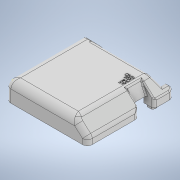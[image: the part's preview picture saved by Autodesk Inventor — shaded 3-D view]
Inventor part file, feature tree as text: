
AUTODESK INVENTOR PART (.ipt)
format: ipt  version: 2022 (Build 260153000, 153)  size: 1,379,840 bytes
history: native  units: mm
features: extrude x58, sketch x43, fillet x10, projected_geometry x2
ambient origin geometry x8: Origin, YZ Plane, XZ Plane, XY Plane, X Axis, Y Axis, Z Axis, Center Point
bodies: Solid1 (feature_tree)
feature tree (113):
  extrude  "Extrusion1"  Depth=62.0mm
  extrude  "Extrusion2"  Depth=3.0mm
  extrude  "Extrusion28"  Depth=3.0mm
  extrude  "Extrusion29"  Depth=4.5mm
  extrude  "Extrusion30"  Depth=3.0mm
  extrude  "Extrusion31"  Depth=54.35mm
  extrude  "Extrusion34"  Depth=51.56mm
  extrude  "Extrusion35"  Depth=6.0mm
  extrude  "Extrusion36"  Depth=6.0mm
  extrude  "Extrusion37"  Depth=20.0mm
  extrude  "Extrusion38"  Depth=1.0mm
  extrude  "Extrusion39"  Depth=2.5mm
  extrude  "Extrusion40"  Depth=2.5mm
  extrude  "Extrusion41"  Depth=3.0mm TaperAngle=0.0deg
  extrude  "Extrusion42"  Depth=8.0mm TaperAngle=0.0deg
  extrude  "Extrusion43"  Depth=8.0mm TaperAngle=0.0deg
  extrude  "Extrusion44"  Depth=2.0mm
  extrude  "Extrusion45"  Depth=4.5mm
  extrude  "Extrusion46"  TaperAngle=0.0deg  [1 undecoded]
  extrude  "Extrusion47"  TaperAngle=0.0deg  [1 undecoded]
  extrude  "Extrusion48"  Depth=2.0mm TaperAngle=0.0deg
  extrude  "Extrusion49"  Depth=10.0mm TaperAngle=0.0deg
  extrude  "Extrusion50"  TaperAngle=0.0deg  [1 undecoded]
  extrude  "Extrusion51"  Depth=2.0mm
  extrude  "Extrusion52"  Depth=3.0mm
  extrude  "Extrusion54"  Depth=3.0mm
  extrude  "Extrusion56"  Depth=2.0mm
  extrude  "Extrusion57"  Depth=2.0mm
  extrude  "Extrusion58"  Depth=2.0mm
  extrude  "Extrusion60"  Depth=8.0mm TaperAngle=0.0deg
  extrude  "Extrusion64"  Depth=4.5mm
  extrude  "Extrusion70"  Depth=4.7mm
  extrude  "Extrusion71"  Depth=100000.0mm TaperAngle=0.0deg
  extrude  "Extrusion72"  Depth=1.0mm
  extrude  "Extrusion73"  Depth=4.7mm
  extrude  "Extrusion74"  Depth=4.7mm
  extrude  "Extrusion75"  Depth=10000.0mm TaperAngle=0.0deg
  extrude  "Extrusion76"  Depth=66.0mm TaperAngle=0.0deg
  extrude  "Extrusion77"  Depth=1000.0mm TaperAngle=0.0deg
  extrude  "Extrusion78"  Depth=67.15mm
  extrude  "Extrusion79"  Depth=1.83mm
  extrude  "Extrusion80"  Depth=1000.0mm TaperAngle=0.0deg
  extrude  "Extrusion81"  Depth=71.5mm
  extrude  "Extrusion82"  Depth=71.5mm
  extrude  "Extrusion83"  Depth=7.0mm TaperAngle=0.0deg
  extrude  "Extrusion84"  Depth=2.0mm
  extrude  "Extrusion85"  Depth=5.0mm TaperAngle=0.0deg
  extrude  "Extrusion86"  Depth=1.0mm TaperAngle=0.0deg
  extrude  "Extrusion89"  TaperAngle=0.0deg  [1 undecoded]
  extrude  "Extrusion90"  Depth=9.0mm
  extrude  "Extrusion91"  Depth=10.0mm TaperAngle=0.0deg
  extrude  "Extrusion92"  Depth=5.65mm
  extrude  "Extrusion93"  Depth=10.0mm TaperAngle=0.0deg
  extrude  "Extrusion94"  Depth=1000.0mm TaperAngle=0.0deg
  extrude  "Extrusion95"  Depth=1000.0mm TaperAngle=0.0deg
  extrude  "Extrusion96"  Depth=1000.0mm TaperAngle=0.0deg
  extrude  "Extrusion97"  Depth=4.0mm
  fillet  "Fillet17"  Radius=1000.0mm
  fillet  "Fillet18"  Radius=4.0mm
  fillet  "Fillet19"  Radius=1000.0mm
  fillet  "Fillet23"  Radius=2.0mm
  fillet  "Fillet26"  Radius=2.0mm
  fillet  "Fillet27"  Radius=2.0mm
  fillet  "Fillet28"  Radius=4.0mm
  fillet  "Fillet29"  Radius=10.0mm
  fillet  "Fillet30"  Radius=1000.0mm
  fillet  "Fillet31"  Radius=2.0mm
  sketch  "Sketch118"  dims[d426=2.0mm d427=0.0mm d432=67.15mm]
  extrude  "Extrusion98"  Depth=2.0mm
  sketch  "Sketch2"  dims[d14=66.0mm d15=62.0mm]
  sketch  "Sketch4"  dims[d16=3.0mm d17=3.0mm]
  sketch  "Sketch38"  dims[d18=3.0mm d19=3.0mm]
  sketch  "Sketch39"  dims[d20=3.0mm d21=4.5mm]
  sketch  "Sketch40"  dims[d22=6.0mm d23=3.0mm]
  sketch  "Sketch47"  dims[d24=57.4mm d25=54.35mm]
  sketch  "Sketch48"  dims[d26=0.8mm d27=51.56mm]
  sketch  "Sketch50"  dims[d28=4.8mm d29=6.0mm]
  sketch  "Sketch51"  dims[d30=6.0mm d31=6.0mm]
  sketch  "Sketch54"  dims[d32=20.0mm d33=20.0mm]
  sketch  "Sketch57"  dims[d34=1.0mm d35=1.0mm]
  sketch  "Sketch59"  dims[d36=2.0mm d37=0.0mm]
  sketch  "Sketch66"  dims[d38=66.0mm d40=3.0mm d41=3.0mm d42=3.0mm d43=3.0mm d44=3.0mm d45=4.5mm d46=6.0mm d47=3.0mm d48=57.4mm d50=0.8mm d51=51.56mm d52=4.8mm d53=6.0mm d54=6.0mm d55=6.0mm d62=18.0mm d63=0.0mm]
  sketch  "Sketch74"  dims[d181=2.0mm d182=2.0mm d184=2.0mm d186=2.0mm d187=8.0mm d190=8.0mm d193=8.0mm d196=8.0mm d329=2.5mm]
  sketch  "Sketch78"  dims[d330=2.5mm d331=2.5mm]
  sketch  "Sketch84"  dims[d332=2.5mm d333=3.0mm d334=0.0mm]
  sketch  "Sketch86"  dims[d336=2.0mm d337=8.0mm d338=0.0mm]
  sketch  "Sketch87"  dims[d339=8.0mm d340=0.0mm d347=8.0mm d348=0.0mm]
  sketch  "Sketch88"  dims[d354=3.0mm d355=0.0mm d359=2.0mm]
  sketch  "Sketch89"  dims[d360=12.0mm d361=4.5mm]
  sketch  "Sketch90"  dims[d362=3.5mm d363=0.0mm]
  sketch  "Sketch91"  dims[d364=3.0mm d365=0.0mm d366=0.0mm]
  sketch  "Sketch93"  dims[d367=2.0mm d368=0.0mm d369=2.0mm d370=0.0mm]
  sketch  "Sketch94"  dims[d371=0.0mm d372=10.0mm d373=0.0mm]
  sketch  "Sketch95"  dims[d374=3.0mm d375=0.0mm]
  sketch  "Sketch96"  dims[d376=2.0mm d377=0.0mm d378=2.0mm]
  projected_geometry  "Projected Loop3"
  sketch  "Sketch97"  dims[d379=19.0mm d380=0.0mm d382=3.0mm]
  projected_geometry  "Projected Loop4"
  sketch  "Sketch98"  dims[d383=3.0mm d384=3.0mm]
  sketch  "Sketch99"  dims[d385=2.0mm d386=0.0mm d387=2.0mm]
  sketch  "Sketch100"  dims[d388=2.0mm d389=2.0mm]
  sketch  "Sketch101"  dims[d390=19.0mm d391=0.0mm d392=2.0mm]
  sketch  "Sketch106"  dims[d393=2.0mm d394=8.0mm d395=0.0mm]
  sketch  "Sketch109"  dims[d396=7.0mm d397=4.5mm]
  sketch  "Sketch110"  dims[d398=16.0mm d399=0.0mm d400=4.7mm]
  sketch  "Sketch111"  dims[d401=0.0mm d402=100000.0mm d403=0.0mm]
  sketch  "Sketch112"  dims[d404=1.0mm d405=1.0mm]
  sketch  "Sketch113"  dims[d406=67.0mm d407=0.0mm d408=4.7mm]
  sketch  "Sketch114"  dims[d409=10000.0mm d410=0.0mm d411=4.7mm]
  sketch  "Sketch115"  dims[d412=10000.0mm d413=0.0mm d414=10000.0mm d415=0.0mm]
  sketch  "Sketch116"  dims[d416=0.349066mm d417=66.0mm d418=0.0mm]
  sketch  "Sketch117"  dims[d419=1000.0mm d420=0.0mm d421=1000.0mm d422=0.0mm]
  sketch  "Sketch119"  dims[d433=1000.0mm d434=0.0mm d437=1.83mm d438=1000.0mm d439=0.0mm d441=71.5mm d442=71.5mm d443=7.0mm d444=0.0mm d447=2.0mm d448=5.0mm d449=0.0mm d473=1.0mm d474=0.0mm d490=0.0mm d491=9.0mm d492=10.0mm d493=0.0mm d495=5.65mm d496=10.0mm d497=0.0mm d498=1000.0mm d499=0.0mm d500=1000.0mm d501=0.0mm d502=1000.0mm d503=0.0mm d504=4.0mm d505=1000.0mm d506=0.0mm d507=4.0mm d508=1000.0mm d509=0.0mm d510=2.0mm d511=2.0mm d512=2.0mm d513=4.0mm d514=10.0mm d515=0.0mm d516=1000.0mm d517=0.0mm d518=2.0mm d519=2.0mm d520=4.0mm d521=1000.0mm d522=0.0mm d523=1.0mm d524=1.0mm d525=15.0mm d526=0.0mm d527=0.0mm d528=1.0mm d529=1.0mm d530=5.0mm d531=0.0mm d532=0.0mm d533=100.0mm d534=0.0mm d535=100.0mm d536=0.0mm d537=100.0mm d538=0.0mm d549=2.6mm d551=2.0mm d552=0.0mm d554=6.0mm d555=6.0mm d556=6.0mm d557=6.0mm d558=7.0mm d559=6.0mm d560=11.8mm d561=6.0mm d562=6.8mm d563=8.14mm d564=6.0mm d565=7.1mm d566=17.55mm d567=0.0mm d572=1000.0mm d573=0.0mm d574=1000.0mm d575=0.0mm d576=10.0mm d577=0.0mm d578=10.0mm d579=0.0mm d580=10.0mm d581=0.0mm d583=4.0mm d584=100.0mm d585=0.0mm d586=100.0mm d587=0.0mm d588=3.0mm d589=3.0mm d590=3.0mm d591=3.0mm d592=6.0mm d593=0.0mm d594=2.8mm d595=0.0mm d596=5.0mm d597=6.0mm d598=2.0mm d599=1.0mm d603=4.0mm d606=2.0mm d607=1.0mm d608=3.0mm d609=2.0mm d610=2.0mm d611=2.0mm d612=10.0mm d613=0.0mm d435=0.872665mm d553=0.5mm]
note: 4 required parameter values undecoded (feature->parameter linkage not recoverable at this tier; creation-order binding heuristic only, values carry confidence <= 0.55)
